# Revit family: Concido Pendant LED - Ceiling based
name_source: partatom
category: Lighting Fixtures
revit_build: Autodesk Revit Architecture 2014 (Build: 20140709_2115(x64)
units: mm (PartAtom-declared; Revit-internal decimal feet)

## types (1)
- Concido Pendant LED
    Apparent Load = 240 VA
    ArticleNumber = See URL hyperlink
    AssetType = Moveable/Fixed
    BIMObjectName = Concido Pendant LED.rfa
    BSAB 96 = SNB.2
    BallastsCELMAEnergyEfficiencyIndex = Class A1/A2
    CCSClassCode = UAC
    CCSClassName = Belysningsarmatur
    CCSTopnode = L
    Color Filter = 16777215
    Colour = White
    ControlGearPosition = Integrated
    Description = 70-80-35 General Lighting Systems
    Diameter 1 = 292 mm
    Dimming Lamp Color Temperature Shift = <None>
    DocumentReference = See URL hyperlink
    Documentation = See URL hyperlink
    Finish = Powder coated
    Frame = Riegens_Aluminum_powder coated white
    Glass = Riegens_Glass_opal
    HasProtectiveEarth = TRUE
    Height 1 = 645 mm
    IP_Code = IP20
    IfcExportAs = IfcLightFixtureType'
    IfcExportType = NOTDEFINED'
    InsulationStandardClass = Class 1
    InternalFuse = Only required in emergency versions
    LampColourRenderingIndex = Ra>80
    LampRating = 63W
    LampType = LED
    LightFixtureMountingType = Suspended
    LightFixturePlacingType = Ceiling
    LightSource = LED 3000K
    LuminairePowerFactor = >0,9
    LuminaireType = Suspended Direct/Indirect LED Luminaire
    Manufacturer = Riegens A/S
    ManufacturerURL = www.riegens.com
    Material = Aluminium and glass
    Model = Concido Pendant LED
    ModelReference = Concido Pendant LED
    NominalVoltage = 220-240V
    Offset from ceiling = 400 mm
    Optic = Direct: Plain mirror reflector.
    PhaseReference = IEC recommendations
    Photometric Web File = Concido Pendant LED DI 63W 3000K.ies
    PhotometricPerformance = In accordance with BS EN 13032-1
    ProductInformation = http://riegens.com
    Shape = Circle
    Size = Ø292 x 645 mm
    Tilt Angle = 90.00°
    TotalWattage = Max. 63W
    URL = http://riegens.com
    Uniclass 1.4 = JY73
    Uniclass2 = Pr_70_70_49_43 Light-Emitting Diode (LED) Luminaires
    Version = v.1.0

## geometry (parser evidence)
native form markers: Sweep x2
no freeform markers — native parametric forms only
